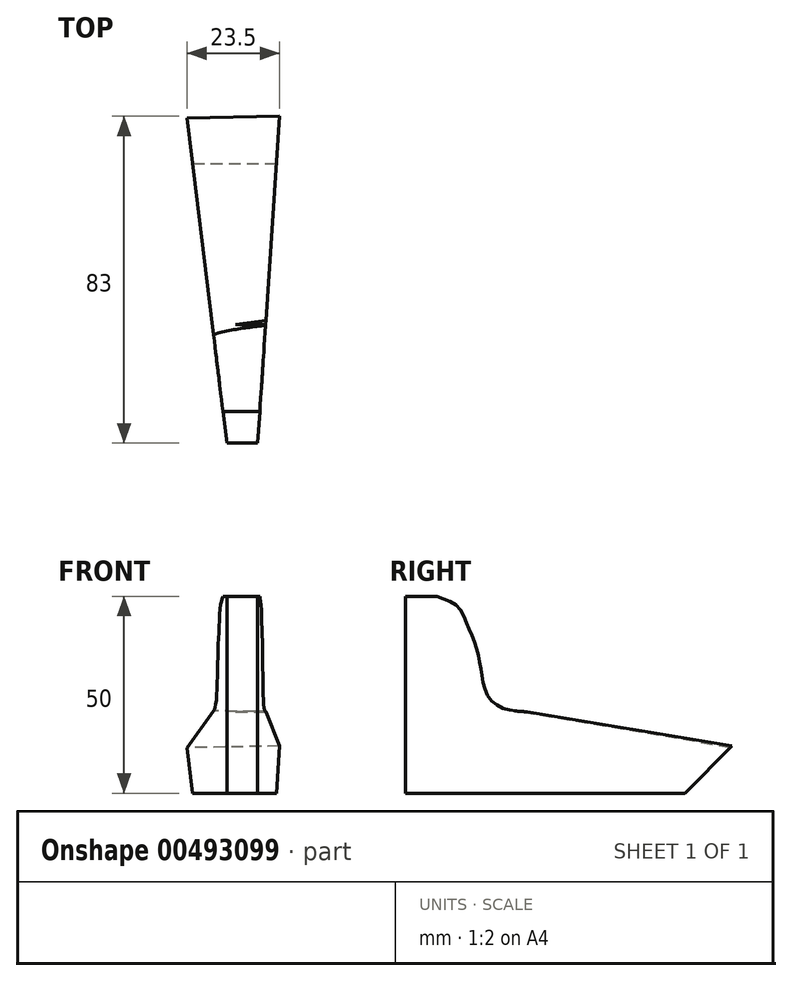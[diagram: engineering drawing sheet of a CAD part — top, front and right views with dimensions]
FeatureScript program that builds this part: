
annotation { "Feature Type Name" : "Feature", "Feature Type Description" : "" }
export const myFeature = defineFeature(function(context is Context, id is Id, definition is map)
    precondition{}
    {
        {
            var Q0;
            Q0=qCreatedBy(makeId("Top.planeOp"),FACE);
            var sketch = newSketch(context, id + "F0", { "sketchPlane" : qUnion([Q0])});
            skLineSegment(sketch, "E0.bottom", {"start": v(-48.56, -73.57) * mm, "end": v(-23.42, -73.57) * mm});
            skLineSegment(sketch, "E0.top", {"start": v(-48.56, 47.45) * mm, "end": v(-23.42, 47.45) * mm});
            skLineSegment(sketch, "E0.left", {"start": v(-48.56, -73.57) * mm, "end": v(-48.56, 47.45) * mm});
            skLineSegment(sketch, "E0.right", {"start": v(-23.42, -73.57) * mm, "end": v(-23.42, 47.45) * mm});
            skSolve(sketch);
        }
        {
            var Q0;
            Q0 = qSketchRegion(id + "F0", true);
            extrude(context, id + "F1", {"entities" : qUnion([Q0]), "depth" : 50 * mm});
        }
        {
            var Q0;
            Q0=makeQuery(id+"F1.opExtrude","CAP_EDGE",EDGE,{"disambiguationData":[OSD([sQuery(id+"F0.wireOp",EDGE,"E0.top")])],"isStart":true});
            chamfer(context, id + "F2", {"entities" : qUnion([Q0]), "width" : 50 * mm, "tangentPropagation" : true});
        }
        {
            var Q0;
            Q0=makeQuery(id+"F1.opExtrude","SWEPT_FACE",FACE,{"disambiguationData":[OSD([sQuery(id+"F0.wireOp",EDGE,"E0.right")])]});
            var sketch = newSketch(context, id + "F3", { "sketchPlane" : qUnion([Q0])});
            skLineSegment(sketch, "E1.bottom", {"start": v(-43.44, 50) * mm, "end": v(48.01, 50) * mm});
            skLineSegment(sketch, "E1.top", {"start": v(-43.44, 20.62) * mm, "end": v(48.01, 20.62) * mm});
            skLineSegment(sketch, "E1.left", {"start": v(-43.44, 50) * mm, "end": v(-43.44, 20.62) * mm});
            skLineSegment(sketch, "E1.right", {"start": v(48.01, 50) * mm, "end": v(48.01, 20.62) * mm});
            skSolve(sketch);
        }
        {
            var Q0;
            Q0 = qSketchRegion(id + "F3", true);
            extrude(context, id + "F4", {"entities" : qUnion([Q0]), "operationType" : NewBodyOperationType.REMOVE, "oppositeDirection" : true, "depth" : 26 * mm});
        }
        {
            var Q0;
            Q0=makeQuery(id+"F1.opExtrude","SWEPT_FACE",FACE,{"disambiguationData":[OSD([sQuery(id+"F0.wireOp",EDGE,"E0.right")])]});
            var sketch = newSketch(context, id + "F5", { "sketchPlane" : qUnion([Q0])});
            skSolve(sketch);
        }
        {
            var Q0;
            {var subQ0=sQuery(id+"F0.wireOp",EDGE,"E0.right");Q0=makeQuery(id+"F5.imprint","IMPRINT",FACE,{"disambiguationData":[TD([[makeQuery(id+"F5.imprint","IMPRINT",EDGE,{"derivedFrom":makeQuery(id+"F1.opExtrude","CAP_EDGE",EDGE,{"disambiguationData":[OSD([subQ0])],"isStart":true})}),1.0]])]});}
            var sketch = newSketch(context, id + "F6", { "sketchPlane" : qUnion([Q0])});
            skFitSpline(sketch, "E2", {"points": [v(-66.47, 50.73) * mm, v(-61.2, 48.11) * mm, v(-58.08, 43.37) * mm, v(-54.96, 34.71) * mm, v(-50.94, 22.81) * mm, v(-33.26, 24.33) * mm, v(-28.44, 42.28) * mm, v(-50.17, 53.51) * mm, v(-66.47, 50.73) * mm]});
            skSolve(sketch);
        }
        {
            var Q0;
            Q0 = qSketchRegion(id + "F6", true);
            extrude(context, id + "F7", {"entities" : qUnion([Q0]), "operationType" : NewBodyOperationType.REMOVE, "oppositeDirection" : true, "depth" : 26 * mm});
        }
        {
            var Q0;
            Q0=qCreatedBy(makeId("Top.planeOp"),FACE);
            var sketch = newSketch(context, id + "F8", { "sketchPlane" : qUnion([Q0])});
            skLineSegment(sketch, "E3", {"start": v(-49.3, 19.84) * mm, "end": v(-37.46, -76.78) * mm});
            skLineSegment(sketch, "E4", {"start": v(-37.46, -76.78) * mm, "end": v(-59.13, -76.78) * mm});
            skLineSegment(sketch, "E5", {"start": v(-59.13, -76.78) * mm, "end": v(-49.3, 19.84) * mm});
            skSolve(sketch);
        }
        {
            var Q0;
            Q0 = qSketchRegion(id + "F8", true);
            extrude(context, id + "F9", {"entities" : qUnion([Q0]), "operationType" : NewBodyOperationType.REMOVE, "depth" : 50 * mm});
        }
        {
            var Q0;
            Q0=qCreatedBy(makeId("Top.planeOp"),FACE);
            var sketch = newSketch(context, id + "F10", { "sketchPlane" : qUnion([Q0])});
            skLineSegment(sketch, "E6", {"start": v(-23.42, 25.26) * mm, "end": v(-30.07, -74.56) * mm});
            skLineSegment(sketch, "E7", {"start": v(-30.07, -74.56) * mm, "end": v(-11.83, -74.56) * mm});
            skLineSegment(sketch, "E8", {"start": v(-11.83, -74.56) * mm, "end": v(-23.42, 25.26) * mm});
            skSolve(sketch);
        }
        {
            var Q0;
            Q0 = qSketchRegion(id + "F10", true);
            extrude(context, id + "F11", {"entities" : qUnion([Q0]), "operationType" : NewBodyOperationType.REMOVE, "depth" : 55 * mm});
        }
        {
            var Q0;
            Q0=makeQuery(id+"F9.boolean.opBoolean","COPY",FACE,{"derivedFrom":makeQuery(id+"F9.opExtrude","SWEPT_FACE",FACE,{"disambiguationData":[OSD([sQuery(id+"F8.wireOp",EDGE,"E3")])]})});
            var sketch = newSketch(context, id + "F12", { "sketchPlane" : qUnion([Q0])});
            skLineSegment(sketch, "E9", {"start": v(-24.72, 9.88) * mm, "end": v(40.76, 20.95) * mm});
            skLineSegment(sketch, "E10", {"start": v(-24.72, 9.88) * mm, "end": v(-24.72, 26.65) * mm});
            skLineSegment(sketch, "E11", {"start": v(-24.72, 26.65) * mm, "end": v(40.76, 20.95) * mm});
            skSolve(sketch);
        }
        {
            var Q0;
            Q0 = qSketchRegion(id + "F12", true);
            extrude(context, id + "F13", {"entities" : qUnion([Q0]), "operationType" : NewBodyOperationType.REMOVE, "oppositeDirection" : true, "depth" : 25 * mm});
        }
    });
